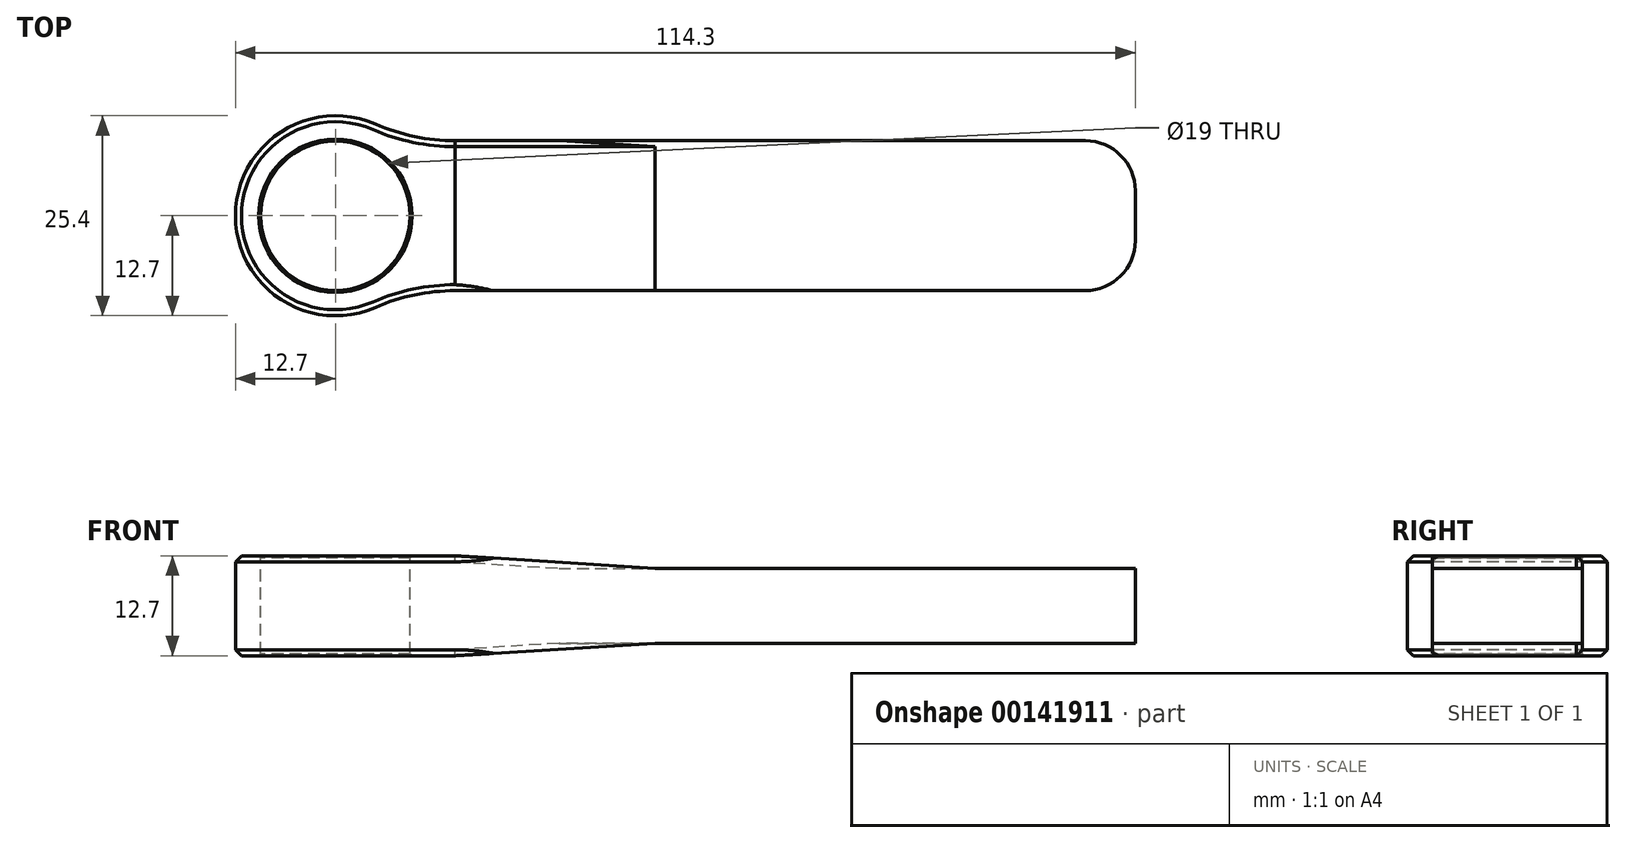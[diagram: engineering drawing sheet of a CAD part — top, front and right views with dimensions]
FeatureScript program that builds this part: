
annotation { "Feature Type Name" : "Feature", "Feature Type Description" : "" }
export const myFeature = defineFeature(function(context is Context, id is Id, definition is map)
    precondition{}
    {
        {
            var Q0;
            Q0=qCreatedBy(makeId("Top.planeOp"),FACE);
            var sketch = newSketch(context, id + "F0", { "sketchPlane" : qUnion([Q0])});
            skCircle(sketch, "E0", {"center": v(0, 0) * mm, "radius": 9.5 * mm});
            skArc(sketch, "E1", {"start": v(5.08, 11.64) * mm, "mid": v(-12.7, 0) * mm, "end": v(5.08, -11.64) * mm});
            skLineSegment(sketch, "E2", {"start": v(0, 0) * mm, "end": v(101.6, 0) * mm});
            skLineSegment(sketch, "E3", {"start": v(101.6, 0) * mm, "end": v(101.6, 3.18) * mm});
            skLineSegment(sketch, "E4", {"start": v(101.6, 0) * mm, "end": v(101.6, -3.17) * mm});
            skLineSegment(sketch, "E5", {"start": v(95.25, -9.52) * mm, "end": v(15.23, -9.52) * mm});
            skLineSegment(sketch, "E6", {"start": v(95.25, 9.53) * mm, "end": v(15.23, 9.53) * mm});
            skPoint(sketch, "E7.visualSharp", {"position": v(101.6, 9.53) * mm});
            skArc(sketch, "E7.filletArc", {"start": v(101.6, 3.18) * mm, "mid": v(99.74, 7.67) * mm, "end": v(95.25, 9.52) * mm});
            skPoint(sketch, "E8.visualSharp", {"position": v(101.6, -9.52) * mm});
            skArc(sketch, "E8.filletArc", {"start": v(95.25, -9.52) * mm, "mid": v(99.74, -7.67) * mm, "end": v(101.6, -3.17) * mm});
            skPoint(sketch, "E9.visualSharp", {"position": v(8.4, 9.53) * mm});
            skArc(sketch, "E9.filletArc", {"start": v(5.08, 11.64) * mm, "mid": v(10.04, 10.06) * mm, "end": v(15.23, 9.52) * mm});
            skPoint(sketch, "E10.visualSharp", {"position": v(8.4, -9.53) * mm});
            skArc(sketch, "E10.filletArc", {"start": v(15.23, -9.52) * mm, "mid": v(10.04, -10.06) * mm, "end": v(5.08, -11.64) * mm});
            skSolve(sketch);
        }
        {
            var Q0;
            Q0 = qSketchRegion(id + "F0", true);
            extrude(context, id + "F1", {"entities" : qUnion([Q0]), "oppositeDirection" : true, "depth" : 12.7 * mm});
        }
        {
            var Q0;
            Q0=makeQuery(id+"F1.opExtrude","SWEPT_FACE",FACE,{"disambiguationData":[OSD([sQuery(id+"F0.wireOp",EDGE,"E5")])]});
            var sketch = newSketch(context, id + "F2", { "sketchPlane" : qUnion([Q0])});
            skLineSegment(sketch, "E11", {"start": v(101.84, -1.59) * mm, "end": v(101.84, 0) * mm});
            skLineSegment(sketch, "E12", {"start": v(100.44, -11.11) * mm, "end": v(40.58, -11.11) * mm});
            skLineSegment(sketch, "E13", {"start": v(101.84, -1.59) * mm, "end": v(40.58, -1.59) * mm});
            skLineSegment(sketch, "E14", {"start": v(15.23, 0) * mm, "end": v(40.58, -1.59) * mm});
            skLineSegment(sketch, "E15", {"start": v(15.23, -12.7) * mm, "end": v(40.58, -11.11) * mm});
            skLineSegment(sketch, "E16", {"start": v(40.58, -11.11) * mm, "end": v(103.13, -11.11) * mm});
            skLineSegment(sketch, "E17", {"start": v(103.13, -11.11) * mm, "end": v(103.13, -14.2) * mm});
            skLineSegment(sketch, "E18", {"start": v(103.13, -14.2) * mm, "end": v(15.28, -14.2) * mm});
            skLineSegment(sketch, "E19", {"start": v(15.28, -14.2) * mm, "end": v(15.23, -12.7) * mm});
            skLineSegment(sketch, "E20", {"start": v(15.23, 0) * mm, "end": v(101.84, 0) * mm});
            skSolve(sketch);
        }
        {
            var Q0;
            Q0 = qSketchRegion(id + "F2", true);
            extrude(context, id + "F3", {"entities" : qUnion([Q0]), "operationType" : NewBodyOperationType.REMOVE, "oppositeDirection" : true, "depth" : 76.2 * mm});
        }
        {
            var Q0;
            Q0=makeQuery(id+"F3.boolean.opBoolean","COPY",EDGE,{"derivedFrom":makeQuery(id+"F3.opExtrude","CAP_EDGE",EDGE,{"disambiguationData":[OSD([sQuery(id+"F2.wireOp",EDGE,"E13")])],"isStart":true})});
            var Q1;
            Q1=makeQuery(id+"F3.boolean.opBoolean","INTERSECT",EDGE,{"derivedFrom":[makeQuery(id+"F1.opExtrude","SWEPT_FACE",FACE,{"disambiguationData":[OSD([sQuery(id+"F0.wireOp",EDGE,"E6")])]}),makeQuery(id+"F3.opExtrude","SWEPT_FACE",FACE,{"disambiguationData":[OSD([sQuery(id+"F2.wireOp",EDGE,"E14")])]})]});
            var Q2;
            Q2=makeQuery(id+"F3.boolean.opBoolean","COPY",EDGE,{"derivedFrom":makeQuery(id+"F3.opExtrude","CAP_EDGE",EDGE,{"disambiguationData":[OSD([sQuery(id+"F2.wireOp",EDGE,"E14")])],"isStart":true})});
            var Q3;
            Q3=makeQuery(id+"F1.opExtrude","CAP_EDGE",EDGE,{"disambiguationData":[OSD([sQuery(id+"F0.wireOp",EDGE,"E1")])],"isStart":true});
            var Q4;
            Q4=makeQuery(id+"F1.opExtrude","CAP_EDGE",EDGE,{"disambiguationData":[OSD([sQuery(id+"F0.wireOp",EDGE,"E10.filletArc")])],"isStart":false});
            var Q5;
            Q5=makeQuery(id+"F3.boolean.opBoolean","COPY",EDGE,{"derivedFrom":makeQuery(id+"F3.opExtrude","CAP_EDGE",EDGE,{"disambiguationData":[OSD([sQuery(id+"F2.wireOp",EDGE,"E15")])],"isStart":true})});
            var Q6;
            Q6=makeQuery(id+"F3.boolean.opBoolean","COPY",EDGE,{"derivedFrom":makeQuery(id+"F3.opExtrude","CAP_EDGE",EDGE,{"disambiguationData":[OSD([sQuery(id+"F2.wireOp",EDGE,"E16")])],"isStart":true})});
            var Q7;
            Q7=makeQuery(id+"F3.boolean.opBoolean","INTERSECT",EDGE,{"derivedFrom":[makeQuery(id+"F1.opExtrude","SWEPT_FACE",FACE,{"disambiguationData":[OSD([sQuery(id+"F0.wireOp",EDGE,"E6")])]}),makeQuery(id+"F3.opExtrude","SWEPT_FACE",FACE,{"disambiguationData":[OSD([sQuery(id+"F2.wireOp",EDGE,"E15")])]})]});
            chamfer(context, id + "F4", {"entities" : qUnion([Q0, Q1, Q2, Q3, Q4, Q5, Q6, Q7]), "width" : 0.76 * mm, "tangentPropagation" : true});
        }
        {
            var Q0;
            Q0=makeQuery(id+"F1.opExtrude","CAP_EDGE",EDGE,{"disambiguationData":[OSD([sQuery(id+"F0.wireOp",EDGE,"E0")])],"isStart":true});
            var Q1;
            Q1=makeQuery(id+"F1.opExtrude","CAP_EDGE",EDGE,{"disambiguationData":[OSD([sQuery(id+"F0.wireOp",EDGE,"E0")])],"isStart":false});
            chamfer(context, id + "F5", {"entities" : qUnion([Q0, Q1]), "width" : 0.25 * mm, "tangentPropagation" : true});
        }
    });
